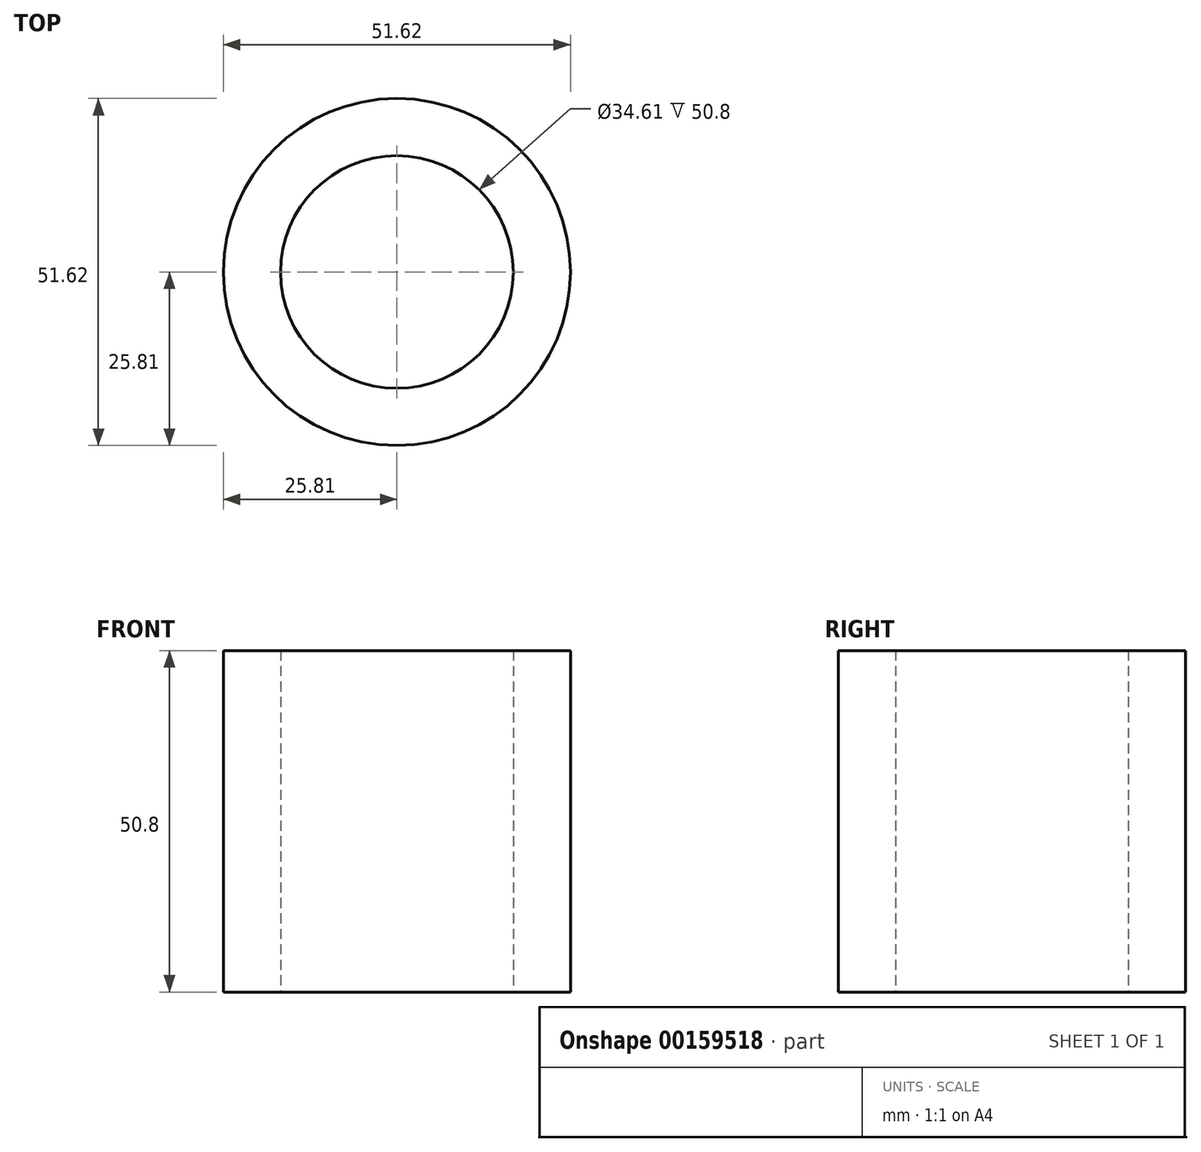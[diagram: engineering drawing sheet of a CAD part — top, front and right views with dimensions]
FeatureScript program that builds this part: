
annotation { "Feature Type Name" : "Feature", "Feature Type Description" : "" }
export const myFeature = defineFeature(function(context is Context, id is Id, definition is map)
    precondition{}
    {
        {
            var Q0;
            Q0=qCreatedBy(makeId("Top.planeOp"),FACE);
            var sketch = newSketch(context, id + "F0", { "sketchPlane" : qUnion([Q0])});
            skCircle(sketch, "E0", {"center": v(0, 0) * mm, "radius": 25.81 * mm});
            skCircle(sketch, "E1", {"center": v(0, 0) * mm, "radius": 17.3 * mm});
            skSolve(sketch);
        }
        {
            var Q0;
            Q0=makeQuery(id+"F0.imprint","IMPRINT",FACE,{"disambiguationData":[TD([[makeQuery(id+"F0.imprint","IMPRINT",EDGE,{"derivedFrom":sQuery(id+"F0.wireOp",EDGE,"E0")}),1.0]])]});
            extrude(context, id + "F1", {"entities" : qUnion([Q0]), "depth" : 50.8 * mm});
        }
    });
